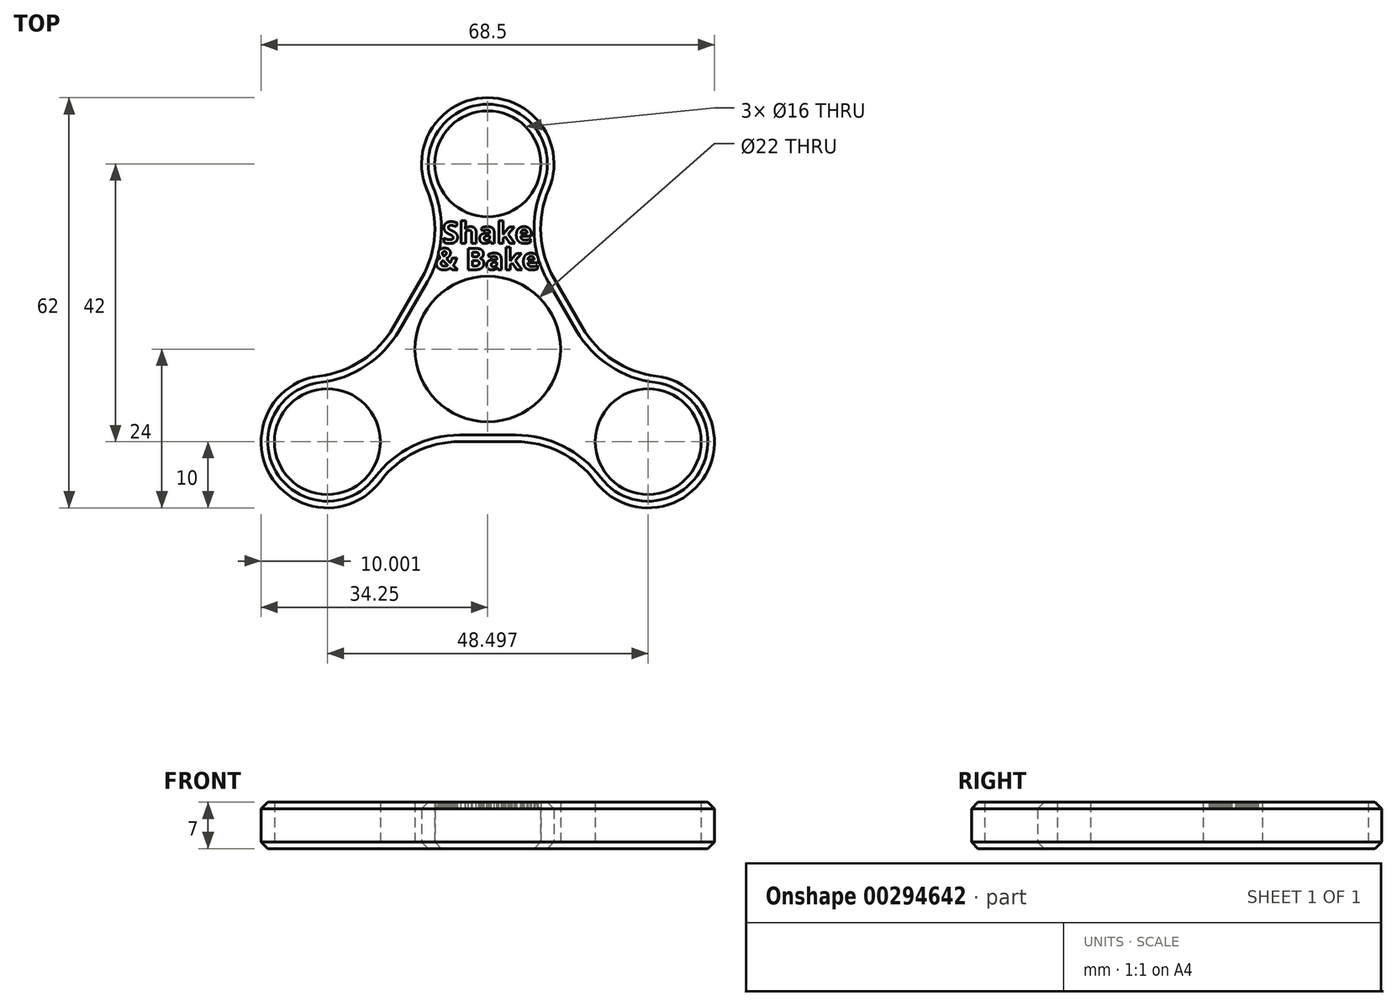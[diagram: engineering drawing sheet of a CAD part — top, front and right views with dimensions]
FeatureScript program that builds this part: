
annotation { "Feature Type Name" : "Feature", "Feature Type Description" : "" }
export const myFeature = defineFeature(function(context is Context, id is Id, definition is map)
    precondition{}
    {
        {
            var Q0;
            Q0=qCreatedBy(makeId("Top.planeOp"),FACE);
            var sketch = newSketch(context, id + "F0", { "sketchPlane" : qUnion([Q0])});
            skCircle(sketch, "E0.cCircle", {"center": v(0, 0) * mm, "radius": 28 * mm, "construction": true});
            skLineSegment(sketch, "E0.0", {"start": v(0, 28) * mm, "end": v(24.25, -14) * mm});
            skLineSegment(sketch, "E0.1", {"start": v(24.25, -14) * mm, "end": v(-24.25, -14) * mm});
            skLineSegment(sketch, "E0.2", {"start": v(-24.25, -14) * mm, "end": v(0, 28) * mm});
            skCircle(sketch, "E1", {"center": v(0, 0) * mm, "radius": 11 * mm});
            skCircle(sketch, "E2", {"center": v(0, 28) * mm, "radius": 8 * mm});
            skCircle(sketch, "E3", {"center": v(24.25, -14) * mm, "radius": 8 * mm});
            skCircle(sketch, "E4", {"center": v(-24.25, -14) * mm, "radius": 8 * mm});
            skCircle(sketch, "E5", {"center": v(0, 28) * mm, "radius": 10 * mm});
            skCircle(sketch, "E6", {"center": v(24.25, -14) * mm, "radius": 10 * mm});
            skCircle(sketch, "E7", {"center": v(-24.25, -14) * mm, "radius": 10 * mm});
            skSolve(sketch);
        }
        {
            var Q0;
            {var subQ0=sQuery(id+"F0.wireOp",EDGE,"E5");var subQ1=sQuery(id+"F0.wireOp",EDGE,"E0.0");var subQ2=makeQuery(id+"F0.imprint","INTERSECT",VERTEX,{"derivedFrom":[subQ1,subQ0]});Q0=makeQuery(id+"F0.imprint","IMPRINT",FACE,{"disambiguationData":[TD([[makeQuery(id+"F0.imprint","IMPRINT",EDGE,{"disambiguationData":[TD([[subQ2,1.0]])],"derivedFrom":subQ1}),1.0]])]});}
            var Q1;
            Q1=makeQuery(id+"F0.imprint","IMPRINT",FACE,{"disambiguationData":[TD([[makeQuery(id+"F0.imprint","IMPRINT",EDGE,{"derivedFrom":sQuery(id+"F0.wireOp",EDGE,"E1")}),-1.0]])]});
            var Q2;
            {var subQ0=sQuery(id+"F0.wireOp",EDGE,"E5");var subQ1=sQuery(id+"F0.wireOp",EDGE,"E0.0");var subQ2=makeQuery(id+"F0.imprint","INTERSECT",VERTEX,{"derivedFrom":[subQ1,subQ0]});Q2=makeQuery(id+"F0.imprint","IMPRINT",FACE,{"disambiguationData":[TD([[makeQuery(id+"F0.imprint","IMPRINT",EDGE,{"disambiguationData":[TD([[subQ2,1.0]])],"derivedFrom":subQ1}),-1.0]])]});}
            var Q3;
            {var subQ0=sQuery(id+"F0.wireOp",EDGE,"E7");var subQ1=sQuery(id+"F0.wireOp",EDGE,"E0.1");var subQ2=makeQuery(id+"F0.imprint","INTERSECT",VERTEX,{"derivedFrom":[subQ1,subQ0]});Q3=makeQuery(id+"F0.imprint","IMPRINT",FACE,{"disambiguationData":[TD([[makeQuery(id+"F0.imprint","IMPRINT",EDGE,{"disambiguationData":[TD([[subQ2,-1.0]])],"derivedFrom":subQ1}),1.0]])]});}
            var Q4;
            {var subQ0=sQuery(id+"F0.wireOp",EDGE,"E7");var subQ1=sQuery(id+"F0.wireOp",EDGE,"E0.1");var subQ2=makeQuery(id+"F0.imprint","INTERSECT",VERTEX,{"derivedFrom":[subQ1,subQ0]});Q4=makeQuery(id+"F0.imprint","IMPRINT",FACE,{"disambiguationData":[TD([[makeQuery(id+"F0.imprint","IMPRINT",EDGE,{"disambiguationData":[TD([[subQ2,-1.0]])],"derivedFrom":subQ1}),-1.0]])]});}
            var Q5;
            {var subQ0=sQuery(id+"F0.wireOp",EDGE,"E6");var subQ1=sQuery(id+"F0.wireOp",EDGE,"E0.0");var subQ2=makeQuery(id+"F0.imprint","INTERSECT",VERTEX,{"derivedFrom":[subQ1,subQ0]});Q5=makeQuery(id+"F0.imprint","IMPRINT",FACE,{"disambiguationData":[TD([[makeQuery(id+"F0.imprint","IMPRINT",EDGE,{"disambiguationData":[TD([[subQ2,-1.0]])],"derivedFrom":subQ1}),-1.0]])]});}
            var Q6;
            {var subQ0=sQuery(id+"F0.wireOp",EDGE,"E6");var subQ1=sQuery(id+"F0.wireOp",EDGE,"E0.0");var subQ2=makeQuery(id+"F0.imprint","INTERSECT",VERTEX,{"derivedFrom":[subQ1,subQ0]});Q6=makeQuery(id+"F0.imprint","IMPRINT",FACE,{"disambiguationData":[TD([[makeQuery(id+"F0.imprint","IMPRINT",EDGE,{"disambiguationData":[TD([[subQ2,-1.0]])],"derivedFrom":subQ1}),1.0]])]});}
            extrude(context, id + "F1", {"entities" : qUnion([Q0, Q1, Q2, Q3, Q4, Q5, Q6]), "depth" : 7 * mm});
        }
        {
            var Q0;
            Q0=makeQuery(id+"F1.opExtrude","SWEPT_EDGE",EDGE,{"disambiguationData":[OSD([sQuery(id+"F0.wireOp",EDGE,"E0.1"),sQuery(id+"F0.wireOp",EDGE,"E6")])]});
            var Q1;
            Q1=makeQuery(id+"F1.opExtrude","SWEPT_EDGE",EDGE,{"disambiguationData":[OSD([sQuery(id+"F0.wireOp",EDGE,"E0.1"),sQuery(id+"F0.wireOp",EDGE,"E7")])]});
            var Q2;
            Q2=makeQuery(id+"F1.opExtrude","SWEPT_EDGE",EDGE,{"disambiguationData":[OSD([sQuery(id+"F0.wireOp",EDGE,"E0.2"),sQuery(id+"F0.wireOp",EDGE,"E7")])]});
            var Q3;
            Q3=makeQuery(id+"F1.opExtrude","SWEPT_EDGE",EDGE,{"disambiguationData":[OSD([sQuery(id+"F0.wireOp",EDGE,"E0.0"),sQuery(id+"F0.wireOp",EDGE,"E5")])]});
            var Q4;
            Q4=makeQuery(id+"F1.opExtrude","SWEPT_EDGE",EDGE,{"disambiguationData":[OSD([sQuery(id+"F0.wireOp",EDGE,"E0.2"),sQuery(id+"F0.wireOp",EDGE,"E5")])]});
            var Q5;
            Q5=makeQuery(id+"F1.opExtrude","SWEPT_EDGE",EDGE,{"disambiguationData":[OSD([sQuery(id+"F0.wireOp",EDGE,"E0.0"),sQuery(id+"F0.wireOp",EDGE,"E6")])]});
            fillet(context, id + "F2", {"entities" : qUnion([Q0, Q1, Q2, Q3, Q4, Q5]), "radius" : 15 * mm, "tangentPropagation" : true, "allowEdgeOverflow" : false});
        }
        {
            var Q0;
            {var subQ0=sQuery(id+"F0.wireOp",EDGE,"E7");var subQ1=sQuery(id+"F0.wireOp",EDGE,"E0.1");Q0=makeQuery(id+"F2.opFillet","BLEND_EDGE",EDGE,{"blendedFrom":[makeQuery(id+"F1.opExtrude","SWEPT_EDGE",EDGE,{"disambiguationData":[OSD([subQ1,subQ0])]}),makeQuery(id+"F1.opExtrude","CAP_FACE",FACE,{"disambiguationData":[OSD([sQuery(id+"F0.wireOp",EDGE,"E0.0"),subQ1,sQuery(id+"F0.wireOp",EDGE,"E0.2"),sQuery(id+"F0.wireOp",EDGE,"E1"),sQuery(id+"F0.wireOp",EDGE,"E2"),sQuery(id+"F0.wireOp",EDGE,"E3"),sQuery(id+"F0.wireOp",EDGE,"E4"),sQuery(id+"F0.wireOp",EDGE,"E5"),sQuery(id+"F0.wireOp",EDGE,"E6"),subQ0])],"isStart":false})],"blendedInto":[makeQuery(id+"F1.opExtrude","CAP_FACE",FACE,{"disambiguationData":[OSD([sQuery(id+"F0.wireOp",EDGE,"E0.0"),subQ1,sQuery(id+"F0.wireOp",EDGE,"E0.2"),sQuery(id+"F0.wireOp",EDGE,"E1"),sQuery(id+"F0.wireOp",EDGE,"E2"),sQuery(id+"F0.wireOp",EDGE,"E3"),sQuery(id+"F0.wireOp",EDGE,"E4"),sQuery(id+"F0.wireOp",EDGE,"E5"),sQuery(id+"F0.wireOp",EDGE,"E6"),subQ0])],"isStart":false})]});}
            var Q1;
            {var subQ0=sQuery(id+"F0.wireOp",EDGE,"E7");var subQ1=sQuery(id+"F0.wireOp",EDGE,"E0.1");Q1=makeQuery(id+"F2.opFillet","BLEND_EDGE",EDGE,{"blendedFrom":[makeQuery(id+"F1.opExtrude","SWEPT_EDGE",EDGE,{"disambiguationData":[OSD([subQ1,subQ0])]}),makeQuery(id+"F1.opExtrude","CAP_FACE",FACE,{"disambiguationData":[OSD([sQuery(id+"F0.wireOp",EDGE,"E0.0"),subQ1,sQuery(id+"F0.wireOp",EDGE,"E0.2"),sQuery(id+"F0.wireOp",EDGE,"E1"),sQuery(id+"F0.wireOp",EDGE,"E2"),sQuery(id+"F0.wireOp",EDGE,"E3"),sQuery(id+"F0.wireOp",EDGE,"E4"),sQuery(id+"F0.wireOp",EDGE,"E5"),sQuery(id+"F0.wireOp",EDGE,"E6"),subQ0])],"isStart":true})],"blendedInto":[makeQuery(id+"F1.opExtrude","CAP_FACE",FACE,{"disambiguationData":[OSD([sQuery(id+"F0.wireOp",EDGE,"E0.0"),subQ1,sQuery(id+"F0.wireOp",EDGE,"E0.2"),sQuery(id+"F0.wireOp",EDGE,"E1"),sQuery(id+"F0.wireOp",EDGE,"E2"),sQuery(id+"F0.wireOp",EDGE,"E3"),sQuery(id+"F0.wireOp",EDGE,"E4"),sQuery(id+"F0.wireOp",EDGE,"E5"),sQuery(id+"F0.wireOp",EDGE,"E6"),subQ0])],"isStart":true})]});}
            chamfer(context, id + "F3", {"entities" : qUnion([Q0, Q1]), "width" : 1 * mm, "tangentPropagation" : true});
        }
        {
            var Q0;
            Q0=makeQuery(id+"F1.opExtrude","CAP_FACE",FACE,{"disambiguationData":[OSD([sQuery(id+"F0.wireOp",EDGE,"E0.0"),sQuery(id+"F0.wireOp",EDGE,"E0.1"),sQuery(id+"F0.wireOp",EDGE,"E0.2"),sQuery(id+"F0.wireOp",EDGE,"E1"),sQuery(id+"F0.wireOp",EDGE,"E2"),sQuery(id+"F0.wireOp",EDGE,"E3"),sQuery(id+"F0.wireOp",EDGE,"E4"),sQuery(id+"F0.wireOp",EDGE,"E5"),sQuery(id+"F0.wireOp",EDGE,"E6"),sQuery(id+"F0.wireOp",EDGE,"E7")])],"isStart":false});
            var sketch = newSketch(context, id + "F4", { "sketchPlane" : qUnion([Q0])});
            skText(sketch, "E8", { "text": "Shake", "fontName": "OpenSans-Bold.ttf"});
            skText(sketch, "E9", { "text": "& Bake", "fontName": "OpenSans-Bold.ttf"});
            const initialGuessF4  = {"E8": [-0.00687, 0.016, 1, 0, 0.00325], "E9": [-0.00794, 0.012, 1, 0, 0.00325]};
            skSetInitialGuess(sketch, initialGuessF4);
            skSolve(sketch);
        }
        {
            var Q0;
            Q0 = qSketchRegion(id + "F4", true);
            extrude(context, id + "F5", {"entities" : qUnion([Q0]), "operationType" : NewBodyOperationType.REMOVE, "oppositeDirection" : true, "depth" : 1 * mm});
        }
    });
